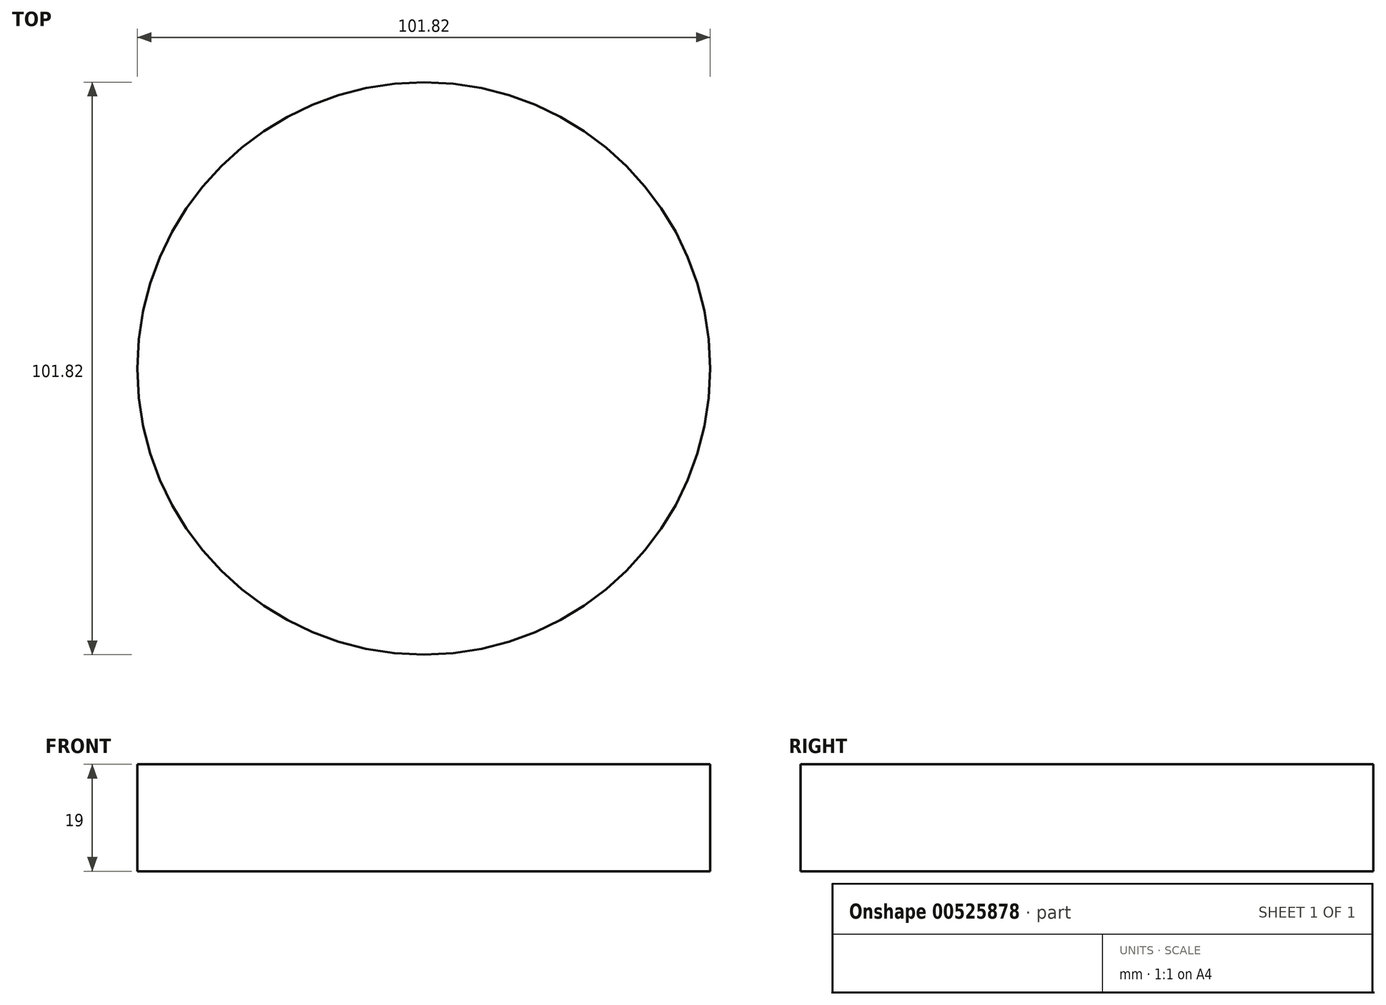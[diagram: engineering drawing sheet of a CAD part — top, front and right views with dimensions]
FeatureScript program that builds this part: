
annotation { "Feature Type Name" : "Feature", "Feature Type Description" : "" }
export const myFeature = defineFeature(function(context is Context, id is Id, definition is map)
    precondition{}
    {
        {
            var Q0;
            Q0=qCreatedBy(makeId("Top.planeOp"),FACE);
            var sketch = newSketch(context, id + "F0", { "sketchPlane" : qUnion([Q0])});
            skCircle(sketch, "E0", {"center": v(0, 0) * mm, "radius": 50.9 * mm});
            skSolve(sketch);
        }
        {
            var Q0;
            Q0=makeQuery(id+"F0.imprint","IMPRINT",FACE,{"disambiguationData":[TD([[makeQuery(id+"F0.imprint","IMPRINT",EDGE,{"derivedFrom":sQuery(id+"F0.wireOp",EDGE,"E0")}),1.0]])]});
            extrude(context, id + "F1", {"entities" : qUnion([Q0]), "depth" : 19 * mm, "offsetDistance" : 25 * mm});
        }
    });
